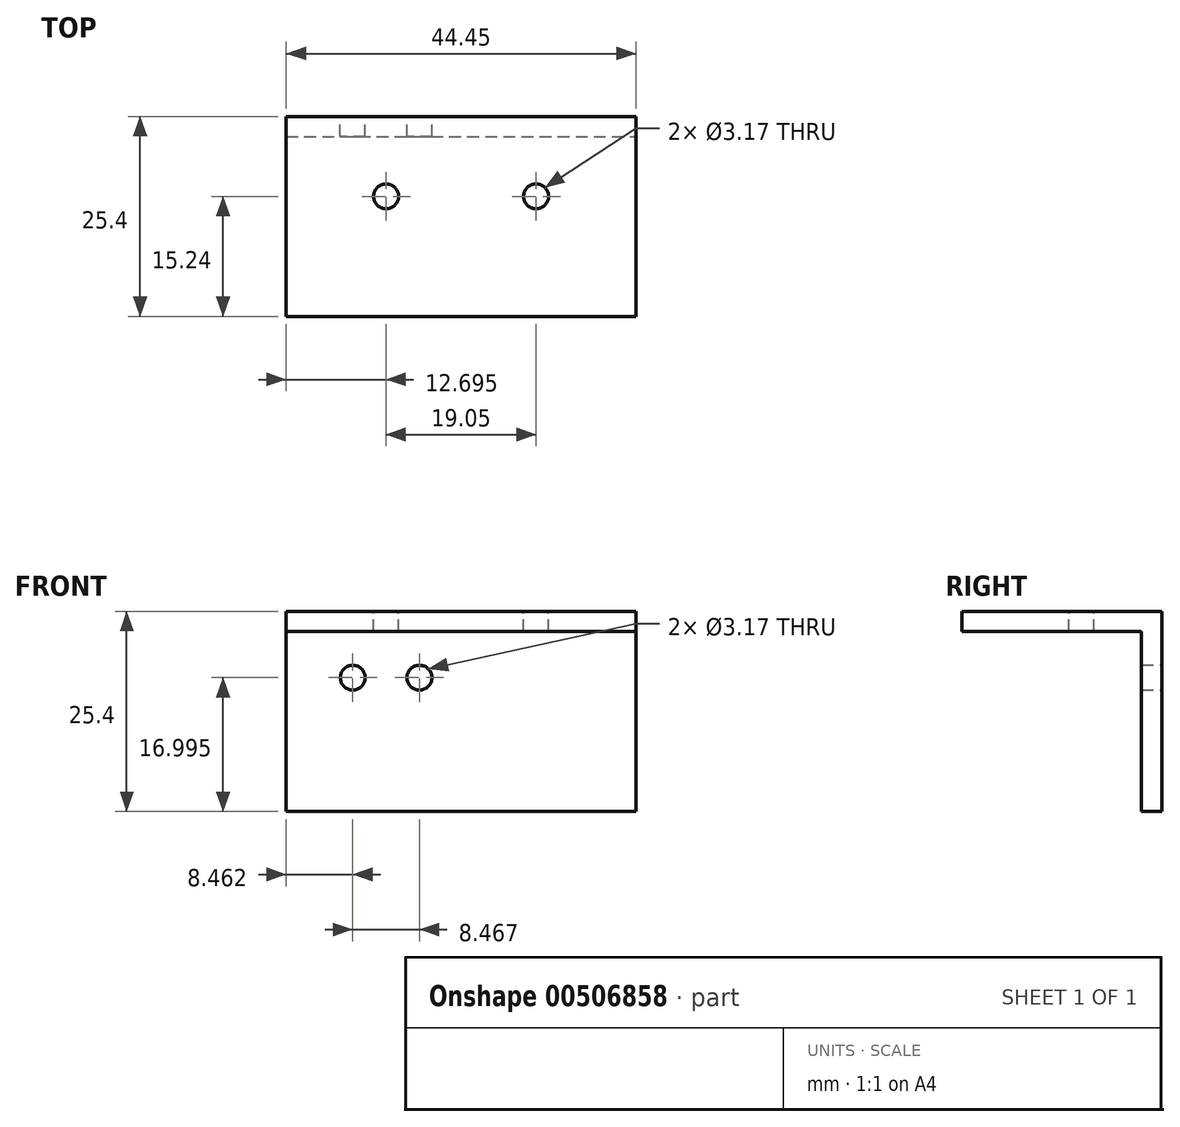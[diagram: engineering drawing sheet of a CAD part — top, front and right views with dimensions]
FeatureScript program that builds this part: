
annotation { "Feature Type Name" : "Feature", "Feature Type Description" : "" }
export const myFeature = defineFeature(function(context is Context, id is Id, definition is map)
    precondition{}
    {
        {
            var Q0;
            Q0=qCreatedBy(makeId("Top.planeOp"),FACE);
            var sketch = newSketch(context, id + "F0", { "sketchPlane" : qUnion([Q0])});
            skLineSegment(sketch, "E0.bottom", {"start": v(-29.82, -8.22) * mm, "end": v(14.63, -8.22) * mm});
            skLineSegment(sketch, "E0.top", {"start": v(-29.82, -33.62) * mm, "end": v(14.63, -33.62) * mm});
            skLineSegment(sketch, "E0.left", {"start": v(-29.82, -8.22) * mm, "end": v(-29.82, -33.62) * mm});
            skLineSegment(sketch, "E0.right", {"start": v(14.63, -8.22) * mm, "end": v(14.63, -33.62) * mm});
            skSolve(sketch);
        }
        {
            var Q0;
            Q0=makeQuery(id+"F0.imprint","IMPRINT",FACE,{"disambiguationData":[TD([[makeQuery(id+"F0.imprint","IMPRINT",EDGE,{"derivedFrom":sQuery(id+"F0.wireOp",EDGE,"E0.bottom")}),-1.0]])]});
            extrude(context, id + "F1", {"entities" : qUnion([Q0]), "depth" : 25.4 * mm, "offsetDistance" : 25.4 * mm});
        }
        {
            var Q0;
            Q0=makeQuery(id+"F1.opExtrude","SWEPT_FACE",FACE,{"disambiguationData":[OSD([sQuery(id+"F0.wireOp",EDGE,"E0.right")])]});
            var Q1;
            Q1=makeQuery(id+"F1.opExtrude","SWEPT_FACE",FACE,{"disambiguationData":[OSD([sQuery(id+"F0.wireOp",EDGE,"E0.left")])]});
            var Q2;
            Q2=makeQuery(id+"F1.opExtrude","SWEPT_FACE",FACE,{"disambiguationData":[OSD([sQuery(id+"F0.wireOp",EDGE,"E0.top")])]});
            var Q3;
            Q3=makeQuery(id+"F1.opExtrude","CAP_FACE",FACE,{"disambiguationData":[OSD([sQuery(id+"F0.wireOp",EDGE,"E0.bottom"),sQuery(id+"F0.wireOp",EDGE,"E0.top"),sQuery(id+"F0.wireOp",EDGE,"E0.left"),sQuery(id+"F0.wireOp",EDGE,"E0.right")])],"isStart":true});
            shell(context, id + "F2", {"entities" : qUnion([Q0, Q1, Q2, Q3]), "thickness" : 2.54 * mm});
        }
        {
            var Q0;
            Q0=qCreatedBy(makeId("Front.planeOp"),FACE);
            var sketch = newSketch(context, id + "F3", { "sketchPlane" : qUnion([Q0])});
            skPoint(sketch, "E1", {"position": v(-12.9, 17) * mm});
            skPoint(sketch, "E2", {"position": v(-21.36, 17) * mm});
            skSolve(sketch);
        }
        {
            var Q0;
            Q0=sQuery(id+"F3.wireOp",VERTEX,"E1");
            var Q1;
            Q1=sQuery(id+"F3.wireOp",VERTEX,"E2");
            var Q2;
            Q2=makeQuery(id+"F1.opExtrude","SWEPT_BODY",BODY,{"disambiguationData":[OSD([sQuery(id+"F0.wireOp",EDGE,"E0.bottom"),sQuery(id+"F0.wireOp",EDGE,"E0.top"),sQuery(id+"F0.wireOp",EDGE,"E0.left"),sQuery(id+"F0.wireOp",EDGE,"E0.right")])]});
            hole(context, id + "F4", {"style" : HoleStyle.SIMPLE, "endStyle" : HoleEndStyle.THROUGH, "oppositeDirection" : true, "holeDiameter" : 3.17 * mm, "majorDiameter" : 6.35 * mm, "isTappedThrough" : true, "tappedDepth" : 12.7 * mm, "tapClearance" : 3, "locations" : qUnion([Q0, Q1]), "scope" : qUnion([Q2])});
        }
        {
            var Q0;
            Q0=makeQuery(id+"F1.opExtrude","CAP_FACE",FACE,{"disambiguationData":[OSD([sQuery(id+"F0.wireOp",EDGE,"E0.bottom"),sQuery(id+"F0.wireOp",EDGE,"E0.top"),sQuery(id+"F0.wireOp",EDGE,"E0.left"),sQuery(id+"F0.wireOp",EDGE,"E0.right")])],"isStart":false});
            var sketch = newSketch(context, id + "F5", { "sketchPlane" : qUnion([Q0])});
            skPoint(sketch, "E3", {"position": v(-17.12, -18.38) * mm});
            skPoint(sketch, "E4", {"position": v(1.93, -18.38) * mm});
            skSolve(sketch);
        }
        {
            var Q0;
            Q0=sQuery(id+"F5.wireOp",VERTEX,"E3");
            var Q1;
            Q1=sQuery(id+"F5.wireOp",VERTEX,"E4");
            var Q2;
            Q2=makeQuery(id+"F1.opExtrude","SWEPT_BODY",BODY,{"disambiguationData":[OSD([sQuery(id+"F0.wireOp",EDGE,"E0.bottom"),sQuery(id+"F0.wireOp",EDGE,"E0.top"),sQuery(id+"F0.wireOp",EDGE,"E0.left"),sQuery(id+"F0.wireOp",EDGE,"E0.right")])]});
            hole(context, id + "F6", {"style" : HoleStyle.SIMPLE, "endStyle" : HoleEndStyle.THROUGH, "holeDiameter" : 3.17 * mm, "majorDiameter" : 6.35 * mm, "isTappedThrough" : true, "tappedDepth" : 12.7 * mm, "tapClearance" : 3, "locations" : qUnion([Q0, Q1]), "scope" : qUnion([Q2])});
        }
    });
